# Revit family: PRD_AR_WtrSplyFitngsForWshBsnsAndTrghs_SelfClosingMixerTap_F3SM1002-1007
name_source: partatom
category: Plumbing Fixtures
revit_build: Autodesk Revit 2018 (Build: 20190510_1515(x64)
units: mm (PartAtom-declared; Revit-internal decimal feet)

## family parameters
Cut with Voids When Loaded = No
Host = Face
OmniClass Number = 23.45.55.14
OmniClass Title = Single Faucets
Part Type = Normal
Room Calculation Point = No
Round Connector Dimension = Use Diameter
Shared = No

## types (6) — shared parameters
AdjustableFlowTime = yes
AssetType = Fixed
Category = Pr_40_20_87_98, Washbasin taps
Color = Chrome
Default Elevation = 850 mm  [stored 2.78871 ft]
Depressurised = no
DiameterNominal = 15.000 mm
DurationUnit = year
FaucetFunction = MIXED
FaucetOperation = SELFCLOSING
FaucetType = PILLAR
Finish = high-polished chromium-plated brass
FlowColdWater = 0.1 L/s
FlowHotWater = 0.1 L/s
FunctionalPrinciple = Hydraulic self-closing
IfcExportAs = IfcValveType
IfcExportType = FAUCET
Manufacturer = KWC Group AG
ManufacturerName = KWC Group AG
ManufacturerURL = www.kwc.com
Material = Brass
MaximumFlowTime = 20.00 seconds
MinimumFlowPressure = 1.00 bar
MinimumFlowTime = 5.00 seconds
NBSDescription = Water supply fittings for wash basins and troughs
NBSReference = 45-35-70/371
OutletMaterial = PRD_AR_SyntheticGrey
ProductInformation = https://pim.kwc.com
ProtectiveShutdown = no
SoundInsulation = no
TapMaterial = PRD_AR_ChromatedBrass_HighPolished
ThermalDisinfection = no
TypeOfMixing = with mixer
TypeOfMounting = WALL-MOUNTING
TypeOfOperation = Manual operation
TypeOfTap = bib tap
URL = www.kwc.com
Uniclass2015Code = Pr_40_20_87_98
Uniclass2015Title = Washbasin taps
Uniclass2015Version = Products v1.10
Version = 1
WarrantyDurationUnit = year
zero-valued in all types: NominalDepth, NominalHeight, NominalWidth

## per-type parameters (varying)
| type | BIMObjectName | DefaultAutomaticHygieneFlushing | Description | GrossWeight | HygieneFlushing | Model | ModelNumber | ModelReference | Name | NetWeight | SpoutProjection | Type | VolumeFlowRate |
| F3SM1002 - 6.0 l/min | PRD_AR_WaterSupplyFittingsForWashBasinsAndTroughs_SelfClosingMixerTap_F3SM1002 |  | F3S-Mix self-closing wall-mounted mixer DN 15 as single-mixer tap for wall mounting with lockable swivelling spout, for sanitary facilities. Self-closing mixing cartridge, hydraulically controlled, piston-free design, self-closing, stepless adjustment of flow duration. With adjustable, turn-proof temperature stop. Connects to hot and cold water. Casing, high-polished chromium-plated brass. Laminar jet controller with integrated flow regulator 6.0 l/min. With adjustable connections, backflow preventer, strainers and screw rosettes. Projection 100 mm. | 2.60 kg | no | F3SM1002 | 2030036195 | F3SM1002 | F3 self-closing mixer tap F3SM1002 | 2.30 kg | 100.00 mm | F3SM1002,5 | 0.10 L/s at 3 bar |
| F3SM1003 - 6.0 l/min | PRD_AR_WaterSupplyFittingsForWashBasinsAndTroughs_SelfClosingMixerTap_F3SM1003 |  | F3S-Mix self-closing wall-mounted mixer DN 15 as single-mixer tap for wall mounting with lockable swivelling spout, for sanitary facilities. Self-closing mixing cartridge, hydraulically controlled, piston-free design, self-closing, stepless adjustment of flow duration. With adjustable, turn-proof temperature stop. Connects to hot and cold water. Casing, high-polished chromium-plated brass. Laminar jet controller with integrated flow regulator 6.0 l/min. With adjustable connections, backflow preventer, strainers and screw rosettes. Projection 160 mm. | 2.80 kg | no | F3SM1003 | 2030036196 | F3SM1003 | F3 self-closing mixer tap F3SM1003 | 2.50 kg | 160.00 mm | F3SM1003,6 | 0.10 L/s at 3 bar |
| F3SM1004 - 6.0 l/min | PRD_AR_WaterSupplyFittingsForWashBasinsAndTroughs_SelfClosingMixerTap_F3SM1004 |  | F3S-Mix self-closing wall-mounted mixer DN 15 as single-mixer tap for wall mounting with lockable swivelling spout, for sanitary facilities. Self-closing mixing cartridge, hydraulically controlled, piston-free design, self-closing, stepless adjustment of flow duration. With adjustable, turn-proof temperature stop. Connects to hot and cold water. Casing, high-polished chromium-plated brass. Laminar jet controller with integrated flow regulator 6.0 l/min. With adjustable connections, backflow preventer, strainers and screw rosettes. Projection 220 mm. | 2.90 kg | no | F3SM1004 | 2030036197 | F3SM1004 | F3 self-closing mixer tap F3SM1004 | 2.70 kg | 220.00 mm | F3SM1004,7 | 0.10 L/s at 3 bar |
| F3SM1005 - 3.0 l/min | PRD_AR_WaterSupplyFittingsForWashBasinsAndTroughs_SelfClosingMixerTap_F3SM1005 |  | F3S-Mix self-closing wall-mounted mixer DN 15 as single-mixer tap for wall mounting with lockable swivelling spout, for sanitary facilities. Self-closing mixing cartridge, hydraulically controlled, piston-free design, self-closing, stepless adjustment of flow duration. With adjustable, turn-proof temperature stop. Connects to hot and cold water. Casing, high-polished chromium-plated brass. Laminar jet controller with integrated flow regulator 3.0 l/min. With adjustable connections, backflow preventer, strainers and screw rosettes. Projection 100 mm. | 2.60 kg | no | F3SM1005 | 2030039562 | F3SM1005 | F3 self-closing mixer tap F3SM1005 | 2.40 kg | 100.00 mm | F3SM1002,5 | 0.05 L/s at 3 bar |
| F3SM1006 - 3.0 l/min | PRD_AR_WaterSupplyFittingsForWashBasinsAndTroughs_SelfClosingMixerTap_F3SM1006 |  | F3S-Mix self-closing wall-mounted mixer DN 15 as single-mixer tap for wall mounting with lockable swivelling spout, for sanitary facilities. Self-closing mixing cartridge, hydraulically controlled, piston-free design, self-closing, stepless adjustment of flow duration. With adjustable, turn-proof temperature stop. Connects to hot and cold water. Casing, high-polished chromium-plated brass. Laminar jet controller with integrated flow regulator 3.0 l/min. With adjustable connections, backflow preventer, strainers and screw rosettes. Projection 160 mm. | 2.70 kg | no | F3SM1006 | 2030040037 | F3SM1006 | F3 self-closing mixer tap F3SM1006 | 2.50 kg | 160.00 mm | F3SM1003,6 | 0.05 L/s at 3 bar |
| F3SM1007 - 3.0 l/min | PRD_AR_WaterSupplyFittingsForWashBasinsAndTroughs_SelfClosingMixerTap_F3SM1007 | 24h after the last activity | F3S-Mix self-closing wall-mounted mixer DN 15 as single-mixer tap for wall mounting with lockable swivelling spout, for sanitary facilities. Self-closing mixing cartridge, hydraulically controlled, piston-free design, self-closing, stepless adjustment of flow duration. With adjustable, turn-proof temperature stop. Connects to hot and cold water. Casing, high-polished chromium-plated brass. Laminar jet controller with integrated flow regulator 3.0 l/min. With adjustable connections, backflow preventer, strainers and screw rosettes. Projection 220 mm. | 2.90 kg | yes | F3SM1007 | 2030040038 | F3SM1007 | F3 self-closing mixer tap F3SM1007 | 2.70 kg | 220.00 mm | F3SM1004,7 | 0.05 L/s at 3 bar |

note: [stored X ft] marks values corroborated as IEEE doubles in the binary element streams (Revit-internal decimal feet)

## geometry (parser evidence)
native form markers: Sweep x10
no freeform markers — native parametric forms only
